# Revit family: Atelier Wall
name_source: partatom
category: Lighting Fixtures
revit_build: Autodesk Revit 2018 (Build: 20170223_1515(x64)
units: mm (PartAtom-declared; Revit-internal decimal feet)

## family parameters
Always vertical = Yes
Cut with Voids When Loaded = No
Host = Wall
Light Source = No
OmniClass Number = 23.80.70.00
OmniClass Title = Lighting
Part Type = Normal
Room Calculation Point = No
Round Connector Dimension = Use Diameter
Shared = No

## types (3) — shared parameters
ADA compliant = N / A
Dimmable = No
Driver Required = No
Efficacy (lm/w) = lamp dependent
Lamp = E27
Location / IP Rating = IP20
Main Material = Metal - Aluminium
Manufacturer = Astro Lighting Ltd
Manufacturer URL - Europe and Rest of World = www.astrolighting.com
Manufacturer URL - North America = us.astrolighting.com
Power (Watts) = 28 W MAX
Product CCT = Lamp Dependent
Product Dimensions (MM) = 185 x 122 mm
Product Location = Wall
Product Name = Atelier Wall
Product URL = https://www.astrolighting.com
Product Weight (KG) = 0.9
URL = www.astrolighting.com
zero-valued in all types: Electrical Class

## per-type parameters (varying)
| type | Main Finish | Product SKU |
| Atelier Wall Black | Matt Black | 1224013 |
| Atelier Wall White | Matt White | 1224012 |
| Atelier Wall Aluminium | Polished Aluminium | 1224011 |

## geometry (parser evidence)
native form markers: Sweep x2
no freeform markers — native parametric forms only
